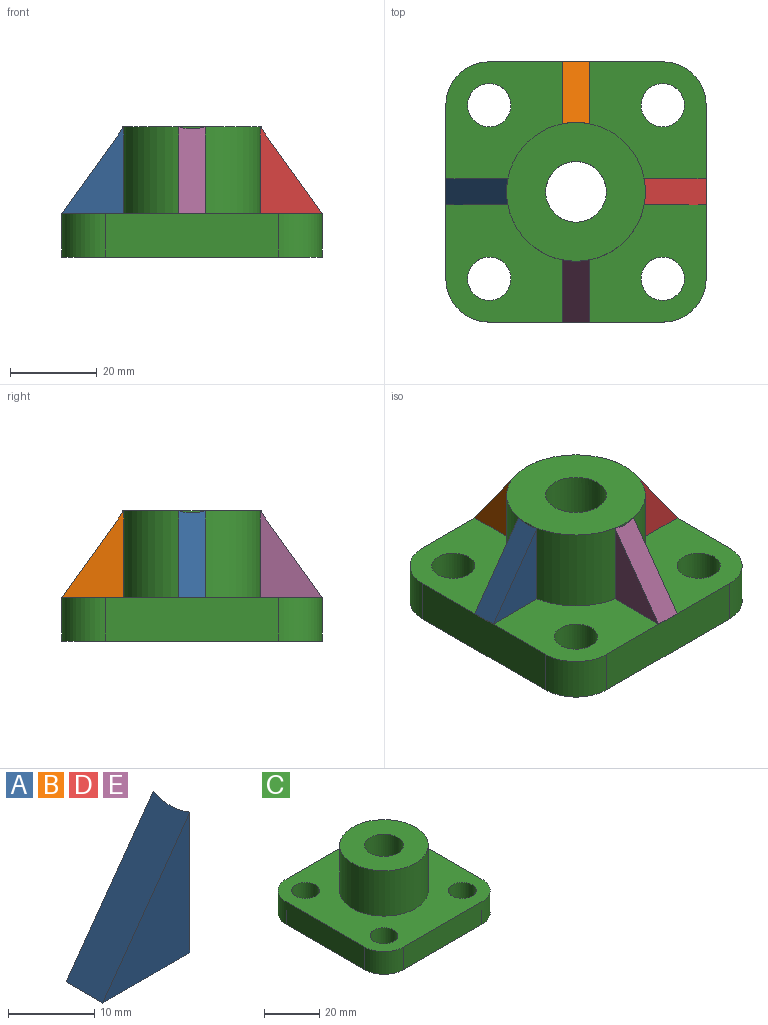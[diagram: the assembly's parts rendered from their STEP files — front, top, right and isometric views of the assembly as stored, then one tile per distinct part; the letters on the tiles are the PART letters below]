
ASSEMBLY  parts=5 mates=1
PART A: 5 faces, bbox 14.3x6x20 mm
  f0: plane 14.28x6mm, normal (0,0,-1), area 84.5mm2, adj f1,f2,f3,f4
  f1: plane 20x14.28mm, normal (0,-1,0), area 142.8mm2, adj f0,f3,f4
  f2: plane 20x14.28mm, normal (0,1,0), area 142.8mm2, adj f0,f3,f4
  f3: plane 20x14.28mm, normal (-0.81,0,0.58), area 145.5mm2, adj f0,f1,f2,f4
  f4: cylinder r=15.71mm len=20mm, axis (0,0,-1), area 119.1mm2, adj f0,f1,f2,f3
PART B: same geometry as A
PART C: 17 faces, bbox 60x60x30 mm
  f0: plane 40x10mm, normal (0,-1,0), area 400mm2, adj f1,f11,f12,f13
  f1: cylinder r=10mm len=10mm, axis (0,0,-1), area 157.1mm2, adj f0,f2,f12,f13
  f2: plane 40x10mm, normal (1,0,0), area 400mm2, adj f1,f3,f12,f13
  f3: cylinder r=10mm len=10mm, axis (0,0,-1), area 157.1mm2, adj f2,f4,f12,f13
  f4: plane 40x10mm, normal (0,1,0), area 400mm2, adj f3,f5,f12,f13
  f5: cylinder r=10mm len=10mm, axis (0,0,-1), area 157.1mm2, adj f4,f6,f12,f13
  f6: plane 40x10mm, normal (-1,0,0), area 400mm2, adj f5,f11,f12,f13
  f7: cylinder r=5mm len=10mm, axis (0,0,-1), area 314.2mm2, adj f12,f13
  f8: cylinder r=5mm len=10mm, axis (0,0,-1), area 314.2mm2, adj f12,f13
  f9: cylinder r=5mm len=10mm, axis (0,0,-1), area 314.2mm2, adj f12,f13
  f10: cylinder r=5mm len=10mm, axis (0,0,-1), area 314.2mm2, adj f12,f13
  f11: cylinder r=10mm len=10mm, axis (0,0,-1), area 157.1mm2, adj f0,f6,f12,f13
  f12: plane 60x60mm, normal (0,0,1), area 2395.8mm2, adj f0,f1,f2,f3,f4,f5,f6,f7
  f13: plane 60x60mm, normal (0,0,-1), area 3046.1mm2, adj f0,f1,f2,f3,f4,f5,f6,f7
  f14: cylinder r=16mm len=32mm, axis (0,0,-1), area 2010.6mm2, adj f12,f15
  f15: plane 32x32mm, normal (0,0,1), area 650.3mm2, adj f14,f16
  f16: cylinder r=7mm len=30mm, axis (0,0,-1), area 1319.5mm2, adj f13,f15
PART D: same geometry as A
PART E: same geometry as A
PLACE A t=(-28.5,7.17,10.65)mm
PLACE B rot(axis=(0,0,-1),90deg) t=(-5.64,30.03,10.65)mm
PLACE C t=(-5.64,7.17,0.65)mm
PLACE D rot(axis=(0,0,1),180deg) t=(17.21,7.17,10.65)mm
PLACE E rot(axis=(0,0,1),90deg) t=(-5.64,-15.68,10.65)mm
MATE fastened A.f0 <-> C.f12  axis (0,0,-1) through (-35.64,7.17,10.65)mm
